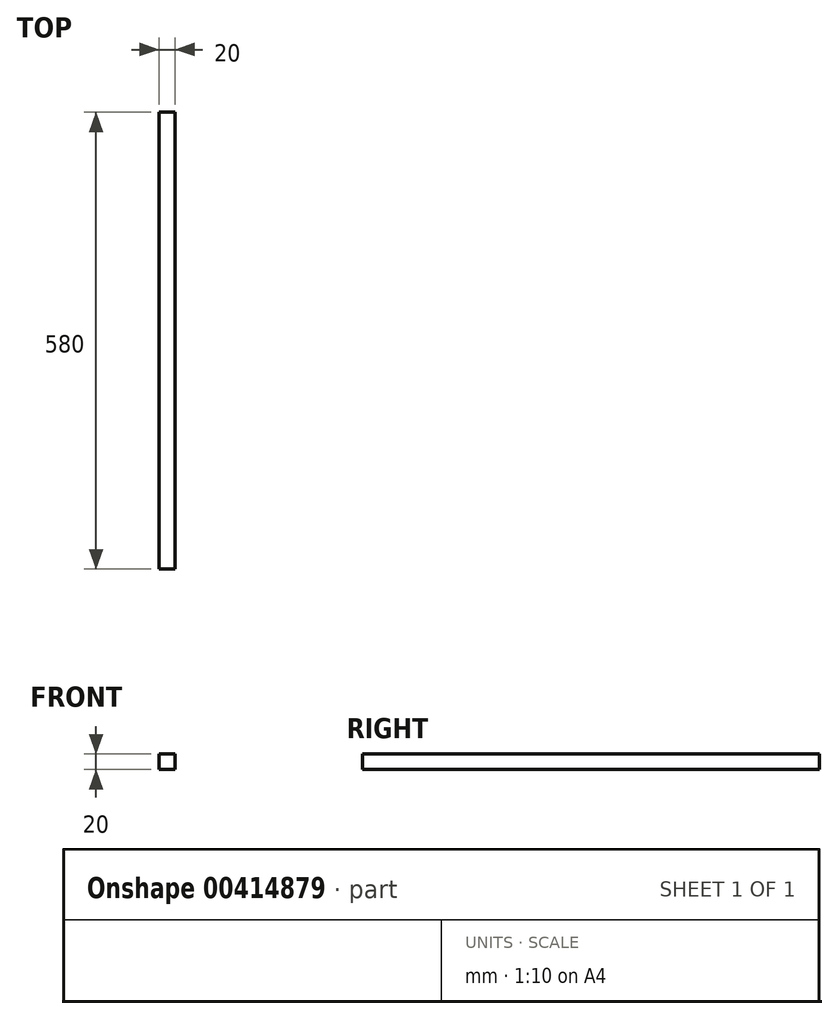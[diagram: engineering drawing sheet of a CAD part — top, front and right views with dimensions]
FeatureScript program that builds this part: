
annotation { "Feature Type Name" : "Feature", "Feature Type Description" : "" }
export const myFeature = defineFeature(function(context is Context, id is Id, definition is map)
    precondition{}
    {
        {
            var Q0;
            Q0=qCreatedBy(makeId("Front.planeOp"),FACE);
            var sketch = newSketch(context, id + "F0", { "sketchPlane" : qUnion([Q0])});
            skLineSegment(sketch, "E0.bottom", {"start": v(-10, 20) * mm, "end": v(10, 20) * mm});
            skLineSegment(sketch, "E0.top", {"start": v(-10, 0) * mm, "end": v(10, 0) * mm});
            skLineSegment(sketch, "E0.left", {"start": v(-10, 20) * mm, "end": v(-10, 0) * mm});
            skLineSegment(sketch, "E0.right", {"start": v(10, 20) * mm, "end": v(10, 0) * mm});
            skSolve(sketch);
        }
        {
            var Q0;
            Q0=makeQuery(id+"F0.imprint","IMPRINT",FACE,{"disambiguationData":[TD([[makeQuery(id+"F0.imprint","IMPRINT",EDGE,{"derivedFrom":sQuery(id+"F0.wireOp",EDGE,"E0.bottom")}),-1.0]])]});
            extrude(context, id + "F1", {"entities" : qUnion([Q0]), "endBound" : BoundingType.SYMMETRIC, "depth" : 580 * mm});
        }
    });
